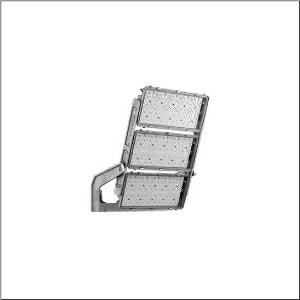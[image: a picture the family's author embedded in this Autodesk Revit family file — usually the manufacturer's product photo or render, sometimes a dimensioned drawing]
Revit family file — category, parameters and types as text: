
# Revit family: floodlight_fl_11_maxi_pro_remote___pl33t_5xa779428t01aa_0213
name_source: partatom
category: Lighting Fixtures
units: mm (PartAtom-declared; Revit-internal decimal feet)

## family parameters
Cut with Voids When Loaded = No
Host = Face
Light Source = No
Part Type = Normal
Room Calculation Point = No
Round Connector Dimension = Use Diameter
Shared = No

## types (1)
- --- (1 x LED, 191730 lm, 1539.6 W, 5700K)
    Apparent Load = 1540 VA
    CIE Flux Codes = 27 70 98 100 100
    Color Rendering = 80
    Color Temperature = 5700K
    Default Elevation = 1800 mm
    Description = Floodlight FL 11  maxi  pro Remote floodlight; light control with lens of PMMA; cover panel of toughened safety glass, transparent; light distribution: PL33T, asymmetric direct distribution, LED; colour temperature: 5700K, rated luminous flux: 191.730lm, colour rendering: CRI > 80, light colour: 857; luminous efficacy: 125lm/W; brightness control: DALI 2 (1 DALI address); with terminal, 8-pole, max. 2.5mm², mains connection: 220..240V/380..400V AC, 50/60Hz, surge voltage resistance: line to ground: 10kV, dimming range 10..100%, dustproof LED module, LED unit replaceable without ESD environment, no afterglow with DALI off / DMX off command, ECG replaceable separately; 1540W floodlight with 3x LED unit of diecast aluminium, coated grey; length: 1.003mm / width: 651mm / height: 338mm; mounting bracket, of diecast aluminium, uncoated, natural, equipment: Power, protection rating (complete): IP66; insulation class (complete): insulation class I (protective earthing); certification: CE, ENEC, VDE; ball protection: ball impact resistant, impact resistance: IK07; only for outdoor installations, rated ambient temperature 10°C, permissible operating ambient temperature: -40..+30°C, permissible storage temperature: -40..+85°Cpackaging unit: 1 piece

Light Distribution: PL33T
    Height = 320 mm
    Lamp = 1 x LED
    Lamp Light Flux = 191730 lm
    Lamp Power = 1539.6 W
    Lamp count = 1
    Length = 1002 mm
    Luminous efficacy = 125 lm/W
    Manufacturer = Siteco
    ModVariant = No
    Model = 5XA779428T01AA
    Mounting Place = Ceiling
    Mounting Type = Surface mounted
    Number of Poles = 1
    OnlyDefault = Yes
    Power Factor = 1
    Product Name = Floodlight FL 11 maxi pro Remote | PL33T
    Product group = floodlight | ceiling mounted
    ProductGroupID = 302
    Protection Class = Protection class I
    Protection Degree = IP 66
    RLX_Detail_Level = 1
    RLX_Emergency_Light_Flux = 0 lm
    RLX_Emergency_Type = 0
    RLX_Emergency_Type_DB = No
    RlxData = <blob elided: 52417 chars, md5=a7e208a6>
    Socket = socket
    Standby Power = 0 W
    System Light Flux = 191730 lm
    System Power = 1540 W
    Type Comments = factory setting: luminous flux: 100 % | dim-lin: 254 | 1080 mA
    Type Image = l_1349141.jpg
    URL = http://relux.com
    VarID = @adj_100453
    Voltage = 0 V
    Weight = 0.00 kg
    Width = 655 mm

## geometry (parser evidence)
native form markers: Blend x4, Sweep x13
no freeform markers — native parametric forms only
